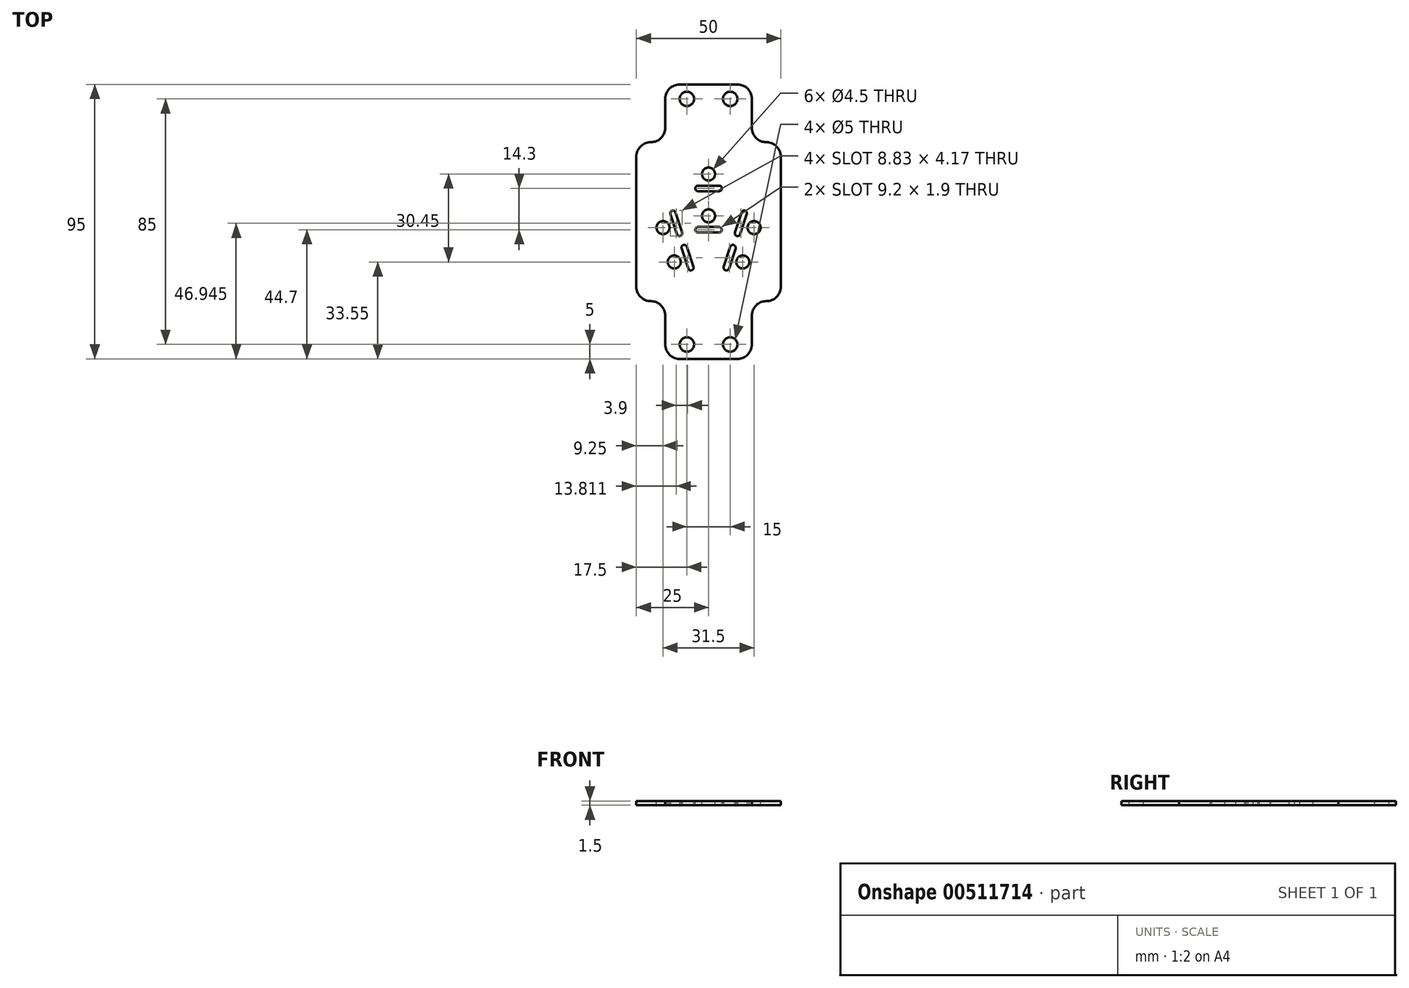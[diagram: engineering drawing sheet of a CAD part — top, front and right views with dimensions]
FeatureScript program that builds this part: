
annotation { "Feature Type Name" : "Feature", "Feature Type Description" : "" }
export const myFeature = defineFeature(function(context is Context, id is Id, definition is map)
    precondition{}
    {
        {
            var Q0;
            Q0=qCreatedBy(makeId("Top.planeOp"),FACE);
            var sketch = newSketch(context, id + "F0", { "sketchPlane" : qUnion([Q0])});
            skLineSegment(sketch, "E0.bottom", {"start": v(-15, 47.5) * mm, "end": v(15, 47.5) * mm});
            skLineSegment(sketch, "E0.top", {"start": v(-15, -47.5) * mm, "end": v(15, -47.5) * mm});
            skLineSegment(sketch, "E0.left", {"start": v(-25, 27.5) * mm, "end": v(-25, -27.5) * mm});
            skLineSegment(sketch, "E0.right", {"start": v(25, 27.5) * mm, "end": v(25, -27.5) * mm});
            skLineSegment(sketch, "E1.top", {"start": v(-25, 27.5) * mm, "end": v(-15, 27.5) * mm});
            skLineSegment(sketch, "E1.right", {"start": v(-15, 47.5) * mm, "end": v(-15, 27.5) * mm});
            skLineSegment(sketch, "E2.top", {"start": v(25, 27.5) * mm, "end": v(15, 27.5) * mm});
            skLineSegment(sketch, "E2.right", {"start": v(15, 47.5) * mm, "end": v(15, 27.5) * mm});
            skLineSegment(sketch, "E3.top", {"start": v(-25, -27.5) * mm, "end": v(-15, -27.5) * mm});
            skLineSegment(sketch, "E3.right", {"start": v(-15, -47.5) * mm, "end": v(-15, -27.5) * mm});
            skLineSegment(sketch, "E4.top", {"start": v(25, -27.5) * mm, "end": v(15, -27.5) * mm});
            skLineSegment(sketch, "E4.right", {"start": v(15, -47.5) * mm, "end": v(15, -27.5) * mm});
            skCircle(sketch, "E5", {"center": v(-7.5, 42.5) * mm, "radius": 2.5 * mm});
            skCircle(sketch, "E6", {"center": v(7.5, 42.5) * mm, "radius": 2.5 * mm});
            skCircle(sketch, "E7", {"center": v(-7.5, -42.5) * mm, "radius": 2.5 * mm});
            skCircle(sketch, "E8", {"center": v(7.5, -42.5) * mm, "radius": 2.5 * mm});
            skSolve(sketch);
        }
        {
            var Q0;
            Q0 = qSketchRegion(id + "F0", true);
            extrude(context, id + "F1", {"entities" : qUnion([Q0]), "depth" : 1.5 * mm});
        }
        {
            var Q0;
            Q0=makeQuery(id+"F1.opExtrude","SWEPT_EDGE",EDGE,{"disambiguationData":[OSD([sQuery(id+"F0.wireOp",EDGE,"E0.bottom"),sQuery(id+"F0.wireOp",EDGE,"E2.right")])]});
            var Q1;
            Q1=makeQuery(id+"F1.opExtrude","SWEPT_EDGE",EDGE,{"disambiguationData":[OSD([sQuery(id+"F0.wireOp",EDGE,"E2.top"),sQuery(id+"F0.wireOp",EDGE,"E2.right")])]});
            var Q2;
            Q2=makeQuery(id+"F1.opExtrude","SWEPT_EDGE",EDGE,{"disambiguationData":[OSD([sQuery(id+"F0.wireOp",EDGE,"E0.right"),sQuery(id+"F0.wireOp",EDGE,"E2.top")])]});
            var Q3;
            Q3=makeQuery(id+"F1.opExtrude","SWEPT_EDGE",EDGE,{"disambiguationData":[OSD([sQuery(id+"F0.wireOp",EDGE,"E0.right"),sQuery(id+"F0.wireOp",EDGE,"E4.top")])]});
            var Q4;
            Q4=makeQuery(id+"F1.opExtrude","SWEPT_EDGE",EDGE,{"disambiguationData":[OSD([sQuery(id+"F0.wireOp",EDGE,"E0.top"),sQuery(id+"F0.wireOp",EDGE,"E4.right")])]});
            var Q5;
            Q5=makeQuery(id+"F1.opExtrude","SWEPT_EDGE",EDGE,{"disambiguationData":[OSD([sQuery(id+"F0.wireOp",EDGE,"E0.bottom"),sQuery(id+"F0.wireOp",EDGE,"E1.right")])]});
            var Q6;
            Q6=makeQuery(id+"F1.opExtrude","SWEPT_EDGE",EDGE,{"disambiguationData":[OSD([sQuery(id+"F0.wireOp",EDGE,"E1.top"),sQuery(id+"F0.wireOp",EDGE,"E1.right")])]});
            var Q7;
            Q7=makeQuery(id+"F1.opExtrude","SWEPT_EDGE",EDGE,{"disambiguationData":[OSD([sQuery(id+"F0.wireOp",EDGE,"E0.left"),sQuery(id+"F0.wireOp",EDGE,"E1.top")])]});
            var Q8;
            Q8=makeQuery(id+"F1.opExtrude","SWEPT_EDGE",EDGE,{"disambiguationData":[OSD([sQuery(id+"F0.wireOp",EDGE,"E0.left"),sQuery(id+"F0.wireOp",EDGE,"E3.top")])]});
            var Q9;
            Q9=makeQuery(id+"F1.opExtrude","SWEPT_EDGE",EDGE,{"disambiguationData":[OSD([sQuery(id+"F0.wireOp",EDGE,"E0.top"),sQuery(id+"F0.wireOp",EDGE,"E3.right")])]});
            var Q10;
            Q10=makeQuery(id+"F1.opExtrude","SWEPT_EDGE",EDGE,{"disambiguationData":[OSD([sQuery(id+"F0.wireOp",EDGE,"E3.top"),sQuery(id+"F0.wireOp",EDGE,"E3.right")])]});
            var Q11;
            Q11=makeQuery(id+"F1.opExtrude","SWEPT_EDGE",EDGE,{"disambiguationData":[OSD([sQuery(id+"F0.wireOp",EDGE,"E4.top"),sQuery(id+"F0.wireOp",EDGE,"E4.right")])]});
            fillet(context, id + "F2", {"entities" : qUnion([Q0, Q1, Q2, Q3, Q4, Q5, Q6, Q7, Q8, Q9, Q10, Q11]), "radius" : 5 * mm, "tangentPropagation" : true, "allowEdgeOverflow" : false});
        }
        {
            var Q0;
            Q0=makeQuery(id+"F1.opExtrude","CAP_FACE",FACE,{"disambiguationData":[OSD([sQuery(id+"F0.wireOp",EDGE,"E0.bottom"),sQuery(id+"F0.wireOp",EDGE,"E0.top"),sQuery(id+"F0.wireOp",EDGE,"E0.left"),sQuery(id+"F0.wireOp",EDGE,"E0.right"),sQuery(id+"F0.wireOp",EDGE,"E1.top"),sQuery(id+"F0.wireOp",EDGE,"E1.right"),sQuery(id+"F0.wireOp",EDGE,"E2.top"),sQuery(id+"F0.wireOp",EDGE,"E2.right"),sQuery(id+"F0.wireOp",EDGE,"E3.top"),sQuery(id+"F0.wireOp",EDGE,"E3.right"),sQuery(id+"F0.wireOp",EDGE,"E4.top"),sQuery(id+"F0.wireOp",EDGE,"E4.right"),sQuery(id+"F0.wireOp",EDGE,"E5"),sQuery(id+"F0.wireOp",EDGE,"E6"),sQuery(id+"F0.wireOp",EDGE,"E7"),sQuery(id+"F0.wireOp",EDGE,"E8")])],"isStart":false});
            var sketch = newSketch(context, id + "F3", { "sketchPlane" : qUnion([Q0])});
            skCircle(sketch, "E9", {"center": v(0, 16.5) * mm, "radius": 2.25 * mm});
            skCircle(sketch, "E10", {"center": v(0, 2) * mm, "radius": 2.25 * mm});
            skCircle(sketch, "E11", {"center": v(15.75, -2.05) * mm, "radius": 2.25 * mm});
            skCircle(sketch, "E12", {"center": v(-15.75, -2.05) * mm, "radius": 2.25 * mm});
            skCircle(sketch, "E13", {"center": v(11.85, -13.95) * mm, "radius": 2.25 * mm});
            skCircle(sketch, "E14", {"center": v(-11.85, -13.95) * mm, "radius": 2.25 * mm});
            skSolve(sketch);
        }
        {
            var Q0;
            Q0 = qSketchRegion(id + "F3", true);
            extrude(context, id + "F4", {"entities" : qUnion([Q0]), "operationType" : NewBodyOperationType.REMOVE, "oppositeDirection" : true, "depth" : 25 * mm});
        }
        {
            var Q0;
            Q0=makeQuery(id+"F1.opExtrude","CAP_FACE",FACE,{"disambiguationData":[OSD([sQuery(id+"F0.wireOp",EDGE,"E0.bottom"),sQuery(id+"F0.wireOp",EDGE,"E0.top"),sQuery(id+"F0.wireOp",EDGE,"E0.left"),sQuery(id+"F0.wireOp",EDGE,"E0.right"),sQuery(id+"F0.wireOp",EDGE,"E1.top"),sQuery(id+"F0.wireOp",EDGE,"E1.right"),sQuery(id+"F0.wireOp",EDGE,"E2.top"),sQuery(id+"F0.wireOp",EDGE,"E2.right"),sQuery(id+"F0.wireOp",EDGE,"E3.top"),sQuery(id+"F0.wireOp",EDGE,"E3.right"),sQuery(id+"F0.wireOp",EDGE,"E4.top"),sQuery(id+"F0.wireOp",EDGE,"E4.right"),sQuery(id+"F0.wireOp",EDGE,"E5"),sQuery(id+"F0.wireOp",EDGE,"E6"),sQuery(id+"F0.wireOp",EDGE,"E7"),sQuery(id+"F0.wireOp",EDGE,"E8")])],"isStart":false});
            var sketch = newSketch(context, id + "F5", { "sketchPlane" : qUnion([Q0])});
            skLineSegment(sketch, "E15", {"start": v(15.75, -2.05) * mm, "end": v(11.85, -13.95) * mm});
            skLineSegment(sketch, "E16", {"start": v(-15.75, -2.05) * mm, "end": v(-11.85, -13.95) * mm});
            skLineSegment(sketch, "E17.bottom", {"start": v(-4.6, 12.45) * mm, "end": v(4.6, 12.45) * mm});
            skLineSegment(sketch, "E17.top", {"start": v(-4.6, 10.55) * mm, "end": v(4.6, 10.55) * mm});
            skLineSegment(sketch, "E17.left", {"start": v(-4.6, 12.45) * mm, "end": v(-4.6, 10.55) * mm});
            skLineSegment(sketch, "E17.right", {"start": v(4.6, 12.45) * mm, "end": v(4.6, 10.55) * mm});
            skLineSegment(sketch, "E18.bottom", {"start": v(-4.6, -1.85) * mm, "end": v(4.6, -1.85) * mm});
            skLineSegment(sketch, "E18.top", {"start": v(-4.6, -3.75) * mm, "end": v(4.6, -3.75) * mm});
            skLineSegment(sketch, "E18.left", {"start": v(-4.6, -1.85) * mm, "end": v(-4.6, -3.75) * mm});
            skLineSegment(sketch, "E18.right", {"start": v(4.6, -1.85) * mm, "end": v(4.6, -3.75) * mm});
            skLineSegment(sketch, "E19", {"start": v(0, 16.5) * mm, "end": v(0, 2) * mm});
            skLineSegment(sketch, "E20", {"start": v(-13.52, 3.52) * mm, "end": v(-10.66, -5.22) * mm});
            skLineSegment(sketch, "E21", {"start": v(-6.76, -17.12) * mm, "end": v(-4.95, -16.53) * mm});
            skLineSegment(sketch, "E22", {"start": v(-4.95, -16.53) * mm, "end": v(-7.82, -7.79) * mm});
            skLineSegment(sketch, "E23", {"start": v(-11.72, 4.11) * mm, "end": v(-13.52, 3.52) * mm});
            skLineSegment(sketch, "E24", {"start": v(13.52, 3.52) * mm, "end": v(10.66, -5.22) * mm});
            skLineSegment(sketch, "E25", {"start": v(6.76, -17.12) * mm, "end": v(4.95, -16.53) * mm});
            skLineSegment(sketch, "E26", {"start": v(4.95, -16.53) * mm, "end": v(7.82, -7.79) * mm});
            skLineSegment(sketch, "E27", {"start": v(11.72, 4.11) * mm, "end": v(13.52, 3.52) * mm});
            skLineSegment(sketch, "E28", {"start": v(8.85, -4.63) * mm, "end": v(10.66, -5.22) * mm});
            skLineSegment(sketch, "E29", {"start": v(7.82, -7.79) * mm, "end": v(9.62, -8.38) * mm});
            skLineSegment(sketch, "E30", {"start": v(-10.66, -5.22) * mm, "end": v(-8.85, -4.63) * mm});
            skLineSegment(sketch, "E31", {"start": v(-7.82, -7.79) * mm, "end": v(-9.62, -8.38) * mm});
            skLineSegment(sketch, "E32.trimOffspring", {"start": v(9.62, -8.38) * mm, "end": v(6.76, -17.12) * mm});
            skLineSegment(sketch, "E33.trimOffspring", {"start": v(8.85, -4.63) * mm, "end": v(11.72, 4.11) * mm});
            skLineSegment(sketch, "E34.trimOffspring", {"start": v(-8.85, -4.63) * mm, "end": v(-11.72, 4.11) * mm});
            skLineSegment(sketch, "E35.trimOffspring", {"start": v(-9.62, -8.38) * mm, "end": v(-6.76, -17.12) * mm});
            skSolve(sketch);
        }
        {
            var Q0;
            Q0 = qSketchRegion(id + "F5", true);
            extrude(context, id + "F6", {"entities" : qUnion([Q0]), "operationType" : NewBodyOperationType.REMOVE, "oppositeDirection" : true, "depth" : 25 * mm});
        }
        {
            var Q0;
            Q0=makeQuery(id+"F6.boolean.opBoolean","COPY",EDGE,{"derivedFrom":makeQuery(id+"F6.opExtrude","SWEPT_EDGE",EDGE,{"disambiguationData":[OSD([sQuery(id+"F5.wireOp",EDGE,"E24"),sQuery(id+"F5.wireOp",EDGE,"E27")])]})});
            var Q1;
            Q1=makeQuery(id+"F6.boolean.opBoolean","COPY",EDGE,{"derivedFrom":makeQuery(id+"F6.opExtrude","SWEPT_EDGE",EDGE,{"disambiguationData":[OSD([sQuery(id+"F5.wireOp",EDGE,"E30"),sQuery(id+"F5.wireOp",EDGE,"E34.trimOffspring")])]})});
            var Q2;
            Q2=makeQuery(id+"F6.boolean.opBoolean","COPY",EDGE,{"derivedFrom":makeQuery(id+"F6.opExtrude","SWEPT_EDGE",EDGE,{"disambiguationData":[OSD([sQuery(id+"F5.wireOp",EDGE,"E29"),sQuery(id+"F5.wireOp",EDGE,"E32.trimOffspring")])]})});
            var Q3;
            Q3=makeQuery(id+"F6.boolean.opBoolean","COPY",EDGE,{"derivedFrom":makeQuery(id+"F6.opExtrude","SWEPT_EDGE",EDGE,{"disambiguationData":[OSD([sQuery(id+"F5.wireOp",EDGE,"E21"),sQuery(id+"F5.wireOp",EDGE,"E22")])]})});
            var Q4;
            Q4=makeQuery(id+"F6.boolean.opBoolean","COPY",EDGE,{"derivedFrom":makeQuery(id+"F6.opExtrude","SWEPT_EDGE",EDGE,{"disambiguationData":[OSD([sQuery(id+"F5.wireOp",EDGE,"E20"),sQuery(id+"F5.wireOp",EDGE,"E23")])]})});
            var Q5;
            Q5=makeQuery(id+"F6.boolean.opBoolean","COPY",EDGE,{"derivedFrom":makeQuery(id+"F6.opExtrude","SWEPT_EDGE",EDGE,{"disambiguationData":[OSD([sQuery(id+"F5.wireOp",EDGE,"E31"),sQuery(id+"F5.wireOp",EDGE,"E35.trimOffspring")])]})});
            var Q6;
            Q6=makeQuery(id+"F6.boolean.opBoolean","COPY",EDGE,{"derivedFrom":makeQuery(id+"F6.opExtrude","SWEPT_EDGE",EDGE,{"disambiguationData":[OSD([sQuery(id+"F5.wireOp",EDGE,"E28"),sQuery(id+"F5.wireOp",EDGE,"E33.trimOffspring")])]})});
            var Q7;
            Q7=makeQuery(id+"F6.boolean.opBoolean","COPY",EDGE,{"derivedFrom":makeQuery(id+"F6.opExtrude","SWEPT_EDGE",EDGE,{"disambiguationData":[OSD([sQuery(id+"F5.wireOp",EDGE,"E25"),sQuery(id+"F5.wireOp",EDGE,"E26")])]})});
            var Q8;
            Q8=makeQuery(id+"F6.boolean.opBoolean","COPY",EDGE,{"derivedFrom":makeQuery(id+"F6.opExtrude","SWEPT_EDGE",EDGE,{"disambiguationData":[OSD([sQuery(id+"F5.wireOp",EDGE,"E17.bottom"),sQuery(id+"F5.wireOp",EDGE,"E17.left")])]})});
            var Q9;
            Q9=makeQuery(id+"F6.boolean.opBoolean","COPY",EDGE,{"derivedFrom":makeQuery(id+"F6.opExtrude","SWEPT_EDGE",EDGE,{"disambiguationData":[OSD([sQuery(id+"F5.wireOp",EDGE,"E18.bottom"),sQuery(id+"F5.wireOp",EDGE,"E18.left")])]})});
            var Q10;
            Q10=makeQuery(id+"F6.boolean.opBoolean","COPY",EDGE,{"derivedFrom":makeQuery(id+"F6.opExtrude","SWEPT_EDGE",EDGE,{"disambiguationData":[OSD([sQuery(id+"F5.wireOp",EDGE,"E23"),sQuery(id+"F5.wireOp",EDGE,"E34.trimOffspring")])]})});
            var Q11;
            Q11=makeQuery(id+"F6.boolean.opBoolean","COPY",EDGE,{"derivedFrom":makeQuery(id+"F6.opExtrude","SWEPT_EDGE",EDGE,{"disambiguationData":[OSD([sQuery(id+"F5.wireOp",EDGE,"E27"),sQuery(id+"F5.wireOp",EDGE,"E33.trimOffspring")])]})});
            var Q12;
            Q12=makeQuery(id+"F6.boolean.opBoolean","COPY",EDGE,{"derivedFrom":makeQuery(id+"F6.opExtrude","SWEPT_EDGE",EDGE,{"disambiguationData":[OSD([sQuery(id+"F5.wireOp",EDGE,"E22"),sQuery(id+"F5.wireOp",EDGE,"E31")])]})});
            var Q13;
            Q13=makeQuery(id+"F6.boolean.opBoolean","COPY",EDGE,{"derivedFrom":makeQuery(id+"F6.opExtrude","SWEPT_EDGE",EDGE,{"disambiguationData":[OSD([sQuery(id+"F5.wireOp",EDGE,"E26"),sQuery(id+"F5.wireOp",EDGE,"E29")])]})});
            var Q14;
            Q14=makeQuery(id+"F6.boolean.opBoolean","COPY",EDGE,{"derivedFrom":makeQuery(id+"F6.opExtrude","SWEPT_EDGE",EDGE,{"disambiguationData":[OSD([sQuery(id+"F5.wireOp",EDGE,"E18.bottom"),sQuery(id+"F5.wireOp",EDGE,"E18.right")])]})});
            var Q15;
            Q15=makeQuery(id+"F6.boolean.opBoolean","COPY",EDGE,{"derivedFrom":makeQuery(id+"F6.opExtrude","SWEPT_EDGE",EDGE,{"disambiguationData":[OSD([sQuery(id+"F5.wireOp",EDGE,"E17.bottom"),sQuery(id+"F5.wireOp",EDGE,"E17.right")])]})});
            var Q16;
            Q16=makeQuery(id+"F6.boolean.opBoolean","COPY",EDGE,{"derivedFrom":makeQuery(id+"F6.opExtrude","SWEPT_EDGE",EDGE,{"disambiguationData":[OSD([sQuery(id+"F5.wireOp",EDGE,"E24"),sQuery(id+"F5.wireOp",EDGE,"E28")])]})});
            var Q17;
            Q17=makeQuery(id+"F6.boolean.opBoolean","COPY",EDGE,{"derivedFrom":makeQuery(id+"F6.opExtrude","SWEPT_EDGE",EDGE,{"disambiguationData":[OSD([sQuery(id+"F5.wireOp",EDGE,"E20"),sQuery(id+"F5.wireOp",EDGE,"E30")])]})});
            var Q18;
            Q18=makeQuery(id+"F6.boolean.opBoolean","COPY",EDGE,{"derivedFrom":makeQuery(id+"F6.opExtrude","SWEPT_EDGE",EDGE,{"disambiguationData":[OSD([sQuery(id+"F5.wireOp",EDGE,"E18.top"),sQuery(id+"F5.wireOp",EDGE,"E18.left")])]})});
            var Q19;
            Q19=makeQuery(id+"F6.boolean.opBoolean","COPY",EDGE,{"derivedFrom":makeQuery(id+"F6.opExtrude","SWEPT_EDGE",EDGE,{"disambiguationData":[OSD([sQuery(id+"F5.wireOp",EDGE,"E17.top"),sQuery(id+"F5.wireOp",EDGE,"E17.left")])]})});
            var Q20;
            Q20=makeQuery(id+"F6.boolean.opBoolean","COPY",EDGE,{"derivedFrom":makeQuery(id+"F6.opExtrude","SWEPT_EDGE",EDGE,{"disambiguationData":[OSD([sQuery(id+"F5.wireOp",EDGE,"E17.top"),sQuery(id+"F5.wireOp",EDGE,"E17.right")])]})});
            var Q21;
            Q21=makeQuery(id+"F6.boolean.opBoolean","COPY",EDGE,{"derivedFrom":makeQuery(id+"F6.opExtrude","SWEPT_EDGE",EDGE,{"disambiguationData":[OSD([sQuery(id+"F5.wireOp",EDGE,"E18.top"),sQuery(id+"F5.wireOp",EDGE,"E18.right")])]})});
            var Q22;
            Q22=makeQuery(id+"F6.boolean.opBoolean","COPY",EDGE,{"derivedFrom":makeQuery(id+"F6.opExtrude","SWEPT_EDGE",EDGE,{"disambiguationData":[OSD([sQuery(id+"F5.wireOp",EDGE,"E21"),sQuery(id+"F5.wireOp",EDGE,"E35.trimOffspring")])]})});
            var Q23;
            Q23=makeQuery(id+"F6.boolean.opBoolean","COPY",EDGE,{"derivedFrom":makeQuery(id+"F6.opExtrude","SWEPT_EDGE",EDGE,{"disambiguationData":[OSD([sQuery(id+"F5.wireOp",EDGE,"E25"),sQuery(id+"F5.wireOp",EDGE,"E32.trimOffspring")])]})});
            fillet(context, id + "F7", {"entities" : qUnion([Q0, Q1, Q2, Q3, Q4, Q5, Q6, Q7, Q8, Q9, Q10, Q11, Q12, Q13, Q14, Q15, Q16, Q17, Q18, Q19, Q20, Q21, Q22, Q23]), "radius" : .95 * mm, "tangentPropagation" : true, "allowEdgeOverflow" : false});
        }
    });
